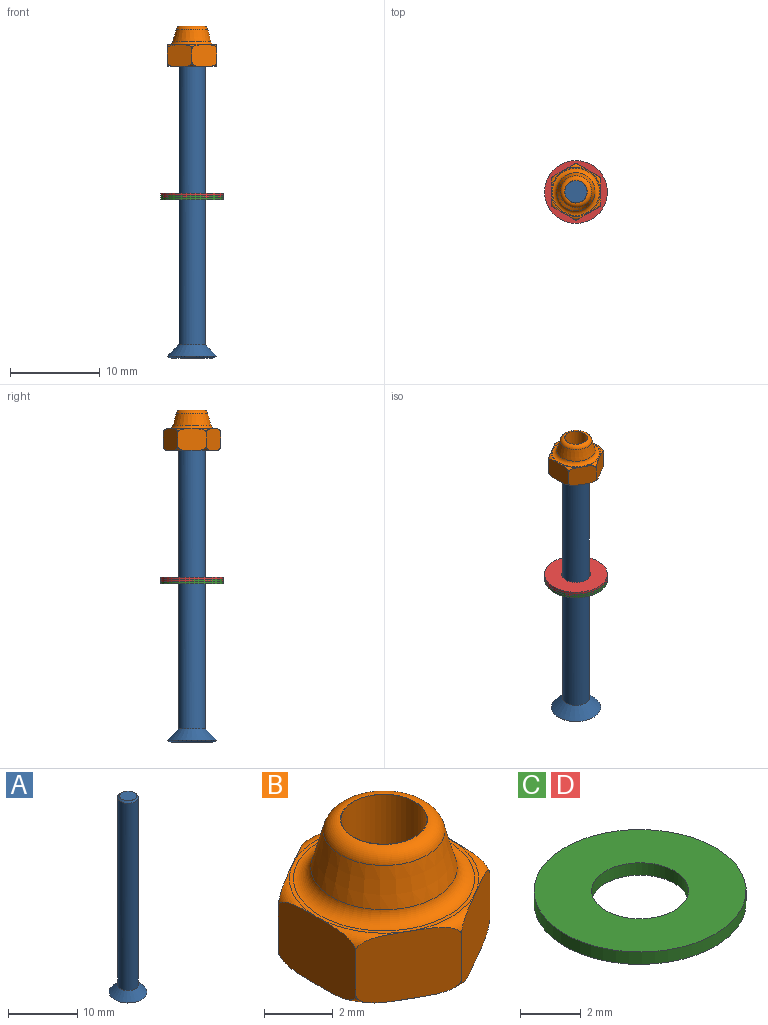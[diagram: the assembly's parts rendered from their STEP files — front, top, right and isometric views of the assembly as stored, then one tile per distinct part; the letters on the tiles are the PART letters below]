
ASSEMBLY  parts=4 mates=3
PART A: 13 faces, bbox 6x6x35 mm
  f0: plane 4.53x4.53mm, normal (0,0,-1), area 11.5mm2, adj f1,f2,f3,f4,f5,f6,f7
  f1: torus R=2.27mm, axis (0,0,1), area 8.5mm2, adj f0,f11
  f2: plane 1.5x1.33mm, normal (-1,0,0), area 2mm2, adj f0,f3,f7,f12
  f3: plane 1.5x1.15mm, normal (-0.5,-0.87,0), area 2mm2, adj f0,f2,f4,f12
  f4: plane 1.5x1.15mm, normal (0.5,-0.87,0), area 2mm2, adj f0,f3,f5,f12
  f5: plane 1.5x1.33mm, normal (1,0,0), area 2mm2, adj f0,f4,f6,f12
  f6: plane 1.5x1.15mm, normal (0.5,0.87,0), area 2mm2, adj f0,f5,f7,f12
  f7: plane 1.5x1.15mm, normal (-0.5,0.87,0), area 2mm2, adj f0,f2,f6,f12
  f8: cone r=1.23mm half-angle=45deg, axis (0,0,-1), area 3.3mm2, adj f9,f10
  f9: plane 2.46x2.46mm, normal (0,0,1), area 4.7mm2, adj f8
  f10: cylinder r=1.5mm len=33.23mm, axis (0,0,-1), area 313.2mm2, adj f8,f11
  f11: cone r=1.5mm half-angle=43.9deg, axis (0,0,-1), area 24.1mm2, adj f1,f10
  f12: plane 2.66x2.3mm, normal (0,0,-1), area 4.6mm2, adj f2,f3,f4,f5,f6,f7
PART B: 15 faces, bbox 6.9x6.9x4.5 mm
  f0: plane 5.49x5.49mm, normal (0,0,1), area 2mm2, adj f1,f12
  f1: torus R=2.75mm, axis (0,0,-1), area 2.8mm2, adj f0,f2,f3,f4,f5,f6,f7
  f2: plane 2.75x2.4mm, normal (0.5,0.87,0), area 7.3mm2, adj f1,f3,f7,f9
  f3: plane 3.18x2.4mm, normal (1,0,0), area 7.3mm2, adj f1,f2,f4,f9
  f4: plane 2.75x2.4mm, normal (0.5,-0.87,0), area 7.3mm2, adj f1,f3,f5,f9
  f5: plane 2.75x2.4mm, normal (-0.5,-0.87,0), area 7.3mm2, adj f1,f4,f6,f9
  f6: plane 3.18x2.4mm, normal (-1,0,0), area 7.3mm2, adj f1,f5,f7,f9
  f7: plane 2.75x2.4mm, normal (-0.5,0.87,0), area 7.3mm2, adj f1,f2,f6,f9
  f8: plane 5.49x5.49mm, normal (0,0,-1), area 18.8mm2, adj f9,f14
  f9: torus R=2.75mm, axis (0,0,-1), area 2.8mm2, adj f2,f3,f4,f5,f6,f7,f8
  f10: cone r=2.23mm half-angle=15deg, axis (0,0,-1), area 16.7mm2, adj f12,f13
  f11: plane 2.52x2.52mm, normal (0,0,1), area 0.1mm2, adj f13,f14
  f12: torus R=2.63mm, axis (0,0,-1), area 10.1mm2, adj f0,f10
  f13: torus R=1.26mm, axis (0,0,1), area 6.7mm2, adj f10,f11
  f14: cylinder r=1.25mm len=4.5mm, axis (0,0,-1), area 35.3mm2, adj f8,f11
PART C: 4 faces, bbox 7x7x0.5 mm
  f0: cylinder r=1.6mm len=3.2mm, axis (0,0,-1), area 5mm2, adj f2,f3
  f1: cylinder r=3.5mm len=7mm, axis (0,0,-1), area 11mm2, adj f2,f3
  f2: plane 7x7mm, normal (0,0,1), area 30.4mm2, adj f0,f1
  f3: plane 7x7mm, normal (0,0,-1), area 30.4mm2, adj f0,f1
PART D: same geometry as C
PLACE A t=(-54.18,-34.32,-100.01)mm
PLACE B t=(25.82,-14.32,-67.53)mm
PLACE C t=(45.82,-24.32,-82.39)mm
PLACE D t=(45.82,-24.32,-82.14)mm
MATE cylindrical D.f0 <-> A.f1  axis (0,0,-1) through (35.82,-34.32,-81.89)mm
MATE cylindrical B.f1 <-> A.f1  axis (0,0,-1) through (35.82,-34.32,-65.28)mm
MATE cylindrical C.f0 <-> A.f1  axis (0,0,-1) through (35.82,-34.32,-81.89)mm
